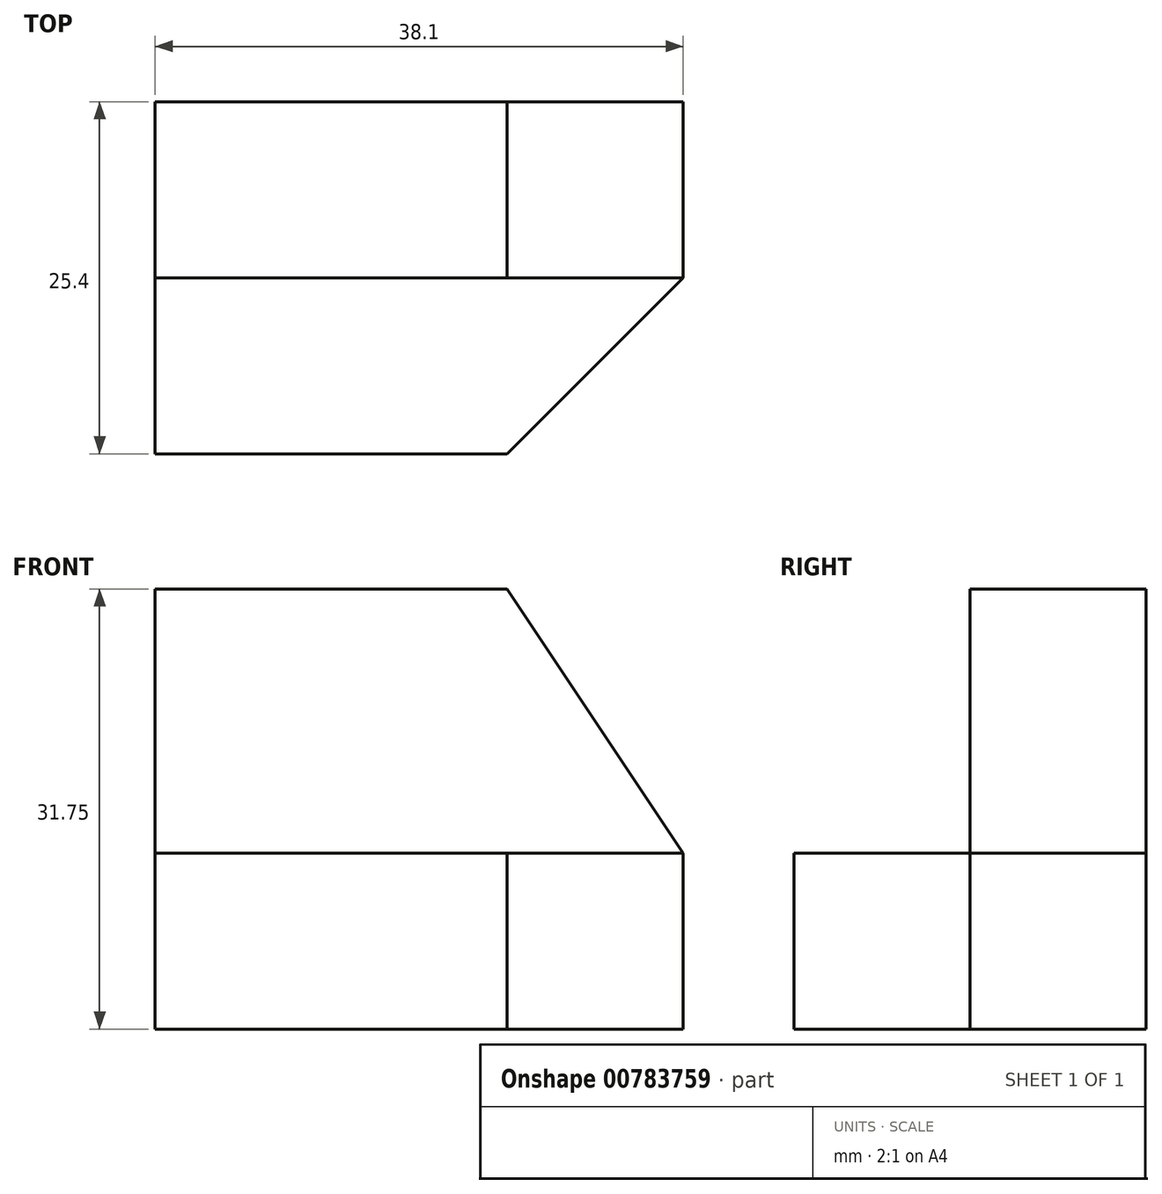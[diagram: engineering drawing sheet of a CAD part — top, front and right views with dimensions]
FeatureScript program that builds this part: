
annotation { "Feature Type Name" : "Feature", "Feature Type Description" : "" }
export const myFeature = defineFeature(function(context is Context, id is Id, definition is map)
    precondition{}
    {
        {
            var Q0;
            Q0=qCreatedBy(makeId("Top.planeOp"),FACE);
            var sketch = newSketch(context, id + "F0", { "sketchPlane" : qUnion([Q0])});
            skLineSegment(sketch, "E0", {"start": v(0, 0) * mm, "end": v(25.4, 0) * mm});
            skLineSegment(sketch, "E1", {"start": v(0, 0) * mm, "end": v(0, 25.4) * mm});
            skLineSegment(sketch, "E2", {"start": v(0, 25.4) * mm, "end": v(38.1, 25.4) * mm});
            skLineSegment(sketch, "E3", {"start": v(38.1, 25.4) * mm, "end": v(38.1, 12.7) * mm});
            skLineSegment(sketch, "E4", {"start": v(25.4, 0) * mm, "end": v(38.1, 12.7) * mm});
            skSolve(sketch);
        }
        {
            var Q0;
            Q0 = qSketchRegion(id + "F0", true);
            extrude(context, id + "F1", {"entities" : qUnion([Q0]), "depth" : 12.7 * mm, "offsetDistance" : 25.4 * mm});
        }
        {
            var Q0;
            Q0=makeQuery(id+"F1.opExtrude","CAP_FACE",FACE,{"disambiguationData":[OSD([sQuery(id+"F0.wireOp",EDGE,"E0"),sQuery(id+"F0.wireOp",EDGE,"E1"),sQuery(id+"F0.wireOp",EDGE,"E2"),sQuery(id+"F0.wireOp",EDGE,"E3"),sQuery(id+"F0.wireOp",EDGE,"E4")])],"isStart":false});
            var sketch = newSketch(context, id + "F2", { "sketchPlane" : qUnion([Q0])});
            skLineSegment(sketch, "E5", {"start": v(38.1, 12.7) * mm, "end": v(0, 12.7) * mm});
            skSolve(sketch);
        }
        {
            var Q0;
            {var subQ0=sQuery(id+"F2.wireOp",EDGE,"E5");Q0=makeQuery(id+"F2.imprint","IMPRINT",FACE,{"disambiguationData":[TD([[makeQuery(id+"F2.imprint","IMPRINT",EDGE,{"derivedFrom":subQ0}),-1.0]])]});}
            extrude(context, id + "F3", {"entities" : qUnion([Q0]), "operationType" : NewBodyOperationType.ADD, "depth" : 19.05 * mm, "offsetDistance" : 25.4 * mm});
        }
        {
            var Q0;
            Q0=makeQuery(id+"F3.opExtrude","SWEPT_FACE",FACE,{"disambiguationData":[OSD([sQuery(id+"F2.wireOp",EDGE,"E5")])]});
            var sketch = newSketch(context, id + "F4", { "sketchPlane" : qUnion([Q0])});
            skLineSegment(sketch, "E6", {"start": v(0, 31.75) * mm, "end": v(25.4, 31.75) * mm});
            skLineSegment(sketch, "E7", {"start": v(25.4, 31.75) * mm, "end": v(38.1, 12.7) * mm});
            skSolve(sketch);
        }
        {
            var Q0;
            {var subQ0=sQuery(id+"F4.wireOp",EDGE,"E7");Q0=makeQuery(id+"F4.imprint","IMPRINT",FACE,{"disambiguationData":[TD([[makeQuery(id+"F4.imprint","IMPRINT",EDGE,{"derivedFrom":subQ0}),1.0]])]});}
            extrude(context, id + "F5", {"entities" : qUnion([Q0]), "operationType" : NewBodyOperationType.REMOVE, "oppositeDirection" : true, "depth" : 12.7 * mm, "offsetDistance" : 25.4 * mm});
        }
    });
